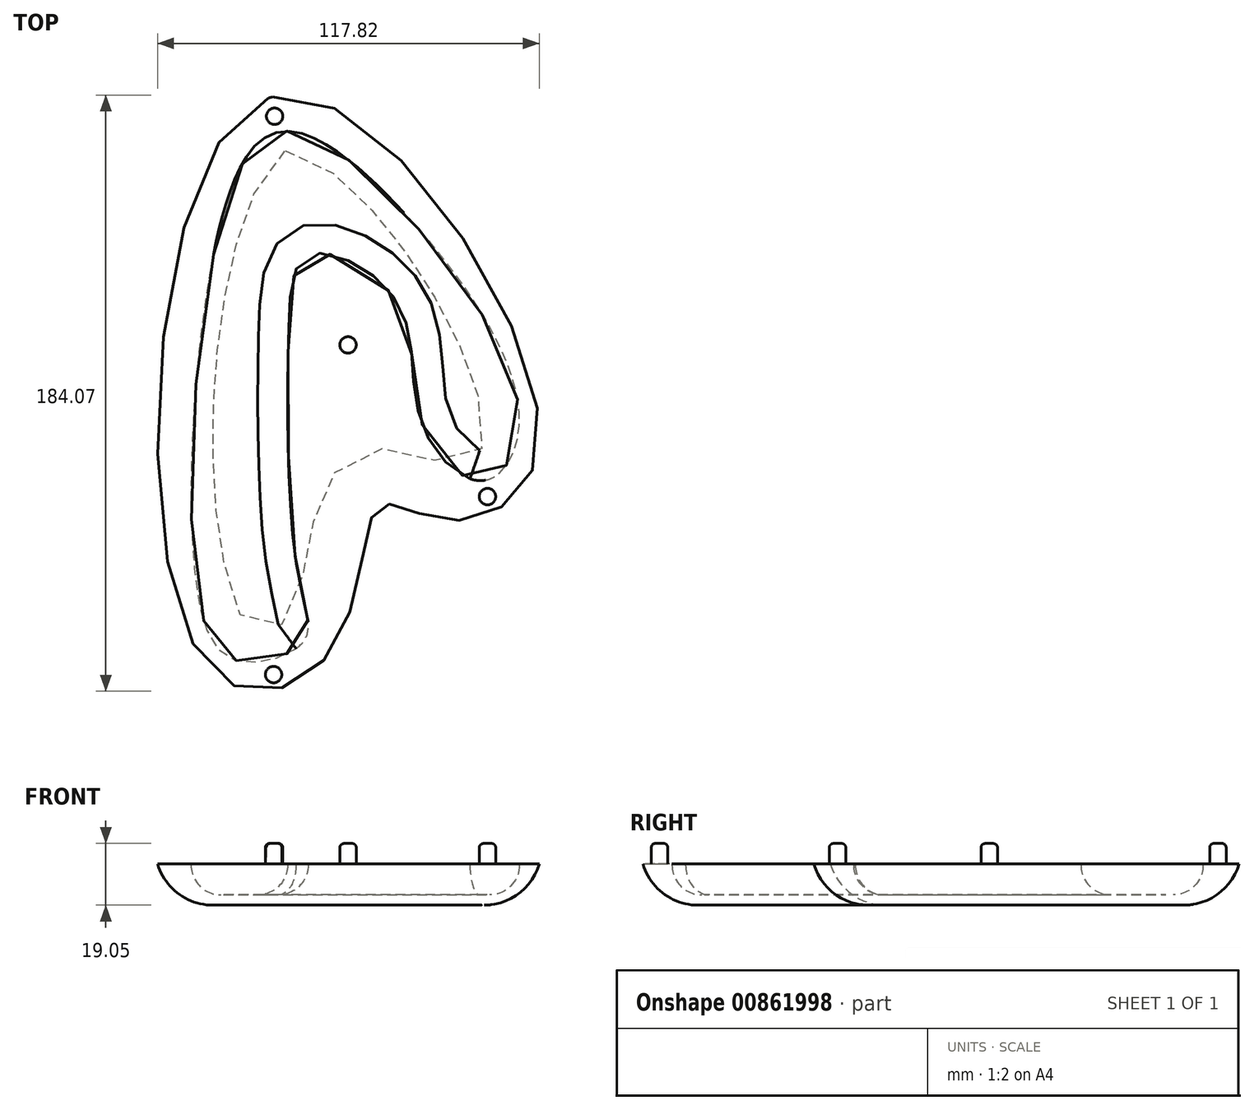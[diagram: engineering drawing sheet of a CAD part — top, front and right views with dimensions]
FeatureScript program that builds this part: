
annotation { "Feature Type Name" : "Feature", "Feature Type Description" : "" }
export const myFeature = defineFeature(function(context is Context, id is Id, definition is map)
    precondition{}
    {
        {
            var Q0;
            Q0=qCreatedBy(makeId("Top.planeOp"),FACE);
            var sketch = newSketch(context, id + "F0", { "sketchPlane" : qUnion([Q0])});
            skLineSegment(sketch, "E0", {"start": v(-51.7, -50.28) * mm, "end": v(-51.7, 51.32) * mm});
            skLineSegment(sketch, "E1", {"start": v(-51.7, 51.32) * mm, "end": v(-41.03, 51.32) * mm});
            skLineSegment(sketch, "E2", {"start": v(-41.03, 51.32) * mm, "end": v(-41.03, -50.28) * mm});
            skLineSegment(sketch, "E3", {"start": v(-41.03, -50.28) * mm, "end": v(-51.7, -50.28) * mm});
            skFitSpline(sketch, "E4", {"points": [v(-56.83, 61.26) * mm, v(-59.56, -52.95) * mm, v(-46.25, -64.69) * mm, v(-28.88, -58.06) * mm, v(-30.58, -38.29) * mm, v(-33.65, 37.4) * mm, v(-26.5, 61.26) * mm, v(0, 46.26) * mm, v(7.26, 9.44) * mm, v(26.35, -8.63) * mm, v(37.6, 11.15) * mm, v(2.49, 73.54) * mm, v(-36.38, 99.1) * mm, v(-56.83, 61.26) * mm]});
            skSolve(sketch);
        }
        {
            var Q0;
            Q0=makeQuery(id+"F0.imprint","IMPRINT",FACE,{"disambiguationData":[TD([[makeQuery(id+"F0.imprint","IMPRINT",EDGE,{"derivedFrom":sQuery(id+"F0.wireOp",EDGE,"E0")}),1.0]])]});
            var Q1;
            Q1=makeQuery(id+"F0.imprint","IMPRINT",FACE,{"disambiguationData":[TD([[makeQuery(id+"F0.imprint","IMPRINT",EDGE,{"derivedFrom":sQuery(id+"F0.wireOp",EDGE,"E0")}),-1.0]])]});
            extrude(context, id + "F1", {"entities" : qUnion([Q0, Q1]), "endBound" : BoundingType.SYMMETRIC, "depth" : 19.05 * mm, "offsetDistance" : 25.4 * mm});
        }
        {
            var Q0;
            Q0=makeQuery(id+"F1.opExtrude","CAP_FACE",FACE,{"disambiguationData":[OSD([sQuery(id+"F0.wireOp",EDGE,"E4")])],"isStart":false});
            fillet(context, id + "F2", {"entities" : qUnion([Q0]), "radius" : 9.22 * mm, "tangentPropagation" : true, "allowEdgeOverflow" : false});
        }
        {
            var Q0;
            Q0=makeQuery(id+"F1.opExtrude","CAP_FACE",FACE,{"disambiguationData":[OSD([sQuery(id+"F0.wireOp",EDGE,"E4")])],"isStart":true});
            fillet(context, id + "F3", {"entities" : qUnion([Q0]), "radius" : 9.22 * mm, "tangentPropagation" : true, "allowEdgeOverflow" : false});
        }
        {
            var Q0;
            Q0=qCreatedBy(makeId("Top.planeOp"),FACE);
            var sketch = newSketch(context, id + "F4", { "sketchPlane" : qUnion([Q0])});
            skFitSpline(sketch, "E5", {"points": [v(-39.96, 109.45) * mm, v(-60.26, -63.74) * mm, v(-19.95, -60.52) * mm, v(-5.79, -16.66) * mm, v(13.96, -20.7) * mm, v(43.72, 4.73) * mm, v(-39.96, 109.45) * mm]});
            skCircle(sketch, "E6", {"center": v(-15.3, 33.26) * mm, "radius": 2.54 * mm});
            skCircle(sketch, "E7", {"center": v(-38.28, -68.53) * mm, "radius": 2.54 * mm});
            skCircle(sketch, "E8", {"center": v(27.76, -13.57) * mm, "radius": 2.54 * mm});
            skCircle(sketch, "E9", {"center": v(-37.98, 103.86) * mm, "radius": 2.54 * mm});
            skSolve(sketch);
        }
        {
            var Q0;
            Q0=makeQuery(id+"F4.imprint","IMPRINT",FACE,{"disambiguationData":[TD([[makeQuery(id+"F4.imprint","IMPRINT",EDGE,{"derivedFrom":sQuery(id+"F4.wireOp",EDGE,"E5")}),1.0]])]});
            var Q1;
            Q1=makeQuery(id+"F4.imprint","IMPRINT",FACE,{"disambiguationData":[TD([[makeQuery(id+"F4.imprint","IMPRINT",EDGE,{"derivedFrom":sQuery(id+"F4.wireOp",EDGE,"E7")}),1.0]])]});
            var Q2;
            Q2=makeQuery(id+"F4.imprint","IMPRINT",FACE,{"disambiguationData":[TD([[makeQuery(id+"F4.imprint","IMPRINT",EDGE,{"derivedFrom":sQuery(id+"F4.wireOp",EDGE,"E6")}),1.0]])]});
            var Q3;
            Q3=makeQuery(id+"F4.imprint","IMPRINT",FACE,{"disambiguationData":[TD([[makeQuery(id+"F4.imprint","IMPRINT",EDGE,{"derivedFrom":sQuery(id+"F4.wireOp",EDGE,"E8")}),1.0]])]});
            var Q4;
            Q4=makeQuery(id+"F4.imprint","IMPRINT",FACE,{"disambiguationData":[TD([[makeQuery(id+"F4.imprint","IMPRINT",EDGE,{"derivedFrom":sQuery(id+"F4.wireOp",EDGE,"E9")}),1.0]])]});
            extrude(context, id + "F5", {"entities" : qUnion([Q0, Q1, Q2, Q3, Q4]), "oppositeDirection" : true, "depth" : 12.7 * mm, "offsetDistance" : 25.4 * mm});
        }
        {
            var Q0;
            Q0=makeQuery(id+"F4.imprint","IMPRINT",FACE,{"disambiguationData":[TD([[makeQuery(id+"F4.imprint","IMPRINT",EDGE,{"derivedFrom":sQuery(id+"F4.wireOp",EDGE,"E7")}),1.0]])]});
            var Q1;
            Q1=makeQuery(id+"F4.imprint","IMPRINT",FACE,{"disambiguationData":[TD([[makeQuery(id+"F4.imprint","IMPRINT",EDGE,{"derivedFrom":sQuery(id+"F4.wireOp",EDGE,"E6")}),1.0]])]});
            var Q2;
            Q2=makeQuery(id+"F4.imprint","IMPRINT",FACE,{"disambiguationData":[TD([[makeQuery(id+"F4.imprint","IMPRINT",EDGE,{"derivedFrom":sQuery(id+"F4.wireOp",EDGE,"E8")}),1.0]])]});
            var Q3;
            Q3=makeQuery(id+"F4.imprint","IMPRINT",FACE,{"disambiguationData":[TD([[makeQuery(id+"F4.imprint","IMPRINT",EDGE,{"derivedFrom":sQuery(id+"F4.wireOp",EDGE,"E9")}),1.0]])]});
            extrude(context, id + "F6", {"entities" : qUnion([Q0, Q1, Q2, Q3]), "operationType" : NewBodyOperationType.ADD, "depth" : 6.35 * mm, "offsetDistance" : 25.4 * mm});
        }
        {
            var Q0;
            Q0=makeQuery(id+"F1.opExtrude","SWEPT_BODY",BODY,{"disambiguationData":[OSD([sQuery(id+"F0.wireOp",EDGE,"E4")])]});
            var Q1;
            Q1=makeQuery(id+"F5.opExtrude","SWEPT_BODY",BODY,{"disambiguationData":[OSD([sQuery(id+"F4.wireOp",EDGE,"E5")])]});
            booleanBodies(context, id + "F7", {"operationType" : BooleanOperationType.SUBTRACTION, "tools" : qUnion([Q0]), "targets" : qUnion([Q1])});
        }
        {
            var Q0;
            Q0=makeQuery(id+"F5.opExtrude","CAP_FACE",FACE,{"disambiguationData":[OSD([sQuery(id+"F4.wireOp",EDGE,"E5")])],"isStart":false});
            fillet(context, id + "F8", {"entities" : qUnion([Q0]), "radius" : 17.78 * mm, "tangentPropagation" : true, "allowEdgeOverflow" : false});
        }
        {
            var Q0;
            Q0=makeQuery(id+"F6.opExtrude","CAP_EDGE",EDGE,{"disambiguationData":[OSD([sQuery(id+"F4.wireOp",EDGE,"E7")])],"isStart":false});
            var Q1;
            Q1=makeQuery(id+"F6.opExtrude","CAP_EDGE",EDGE,{"disambiguationData":[OSD([sQuery(id+"F4.wireOp",EDGE,"E6")])],"isStart":false});
            var Q2;
            Q2=makeQuery(id+"F6.opExtrude","CAP_EDGE",EDGE,{"disambiguationData":[OSD([sQuery(id+"F4.wireOp",EDGE,"E8")])],"isStart":false});
            var Q3;
            Q3=makeQuery(id+"F6.opExtrude","CAP_EDGE",EDGE,{"disambiguationData":[OSD([sQuery(id+"F4.wireOp",EDGE,"E9")])],"isStart":false});
            fillet(context, id + "F9", {"entities" : qUnion([Q0, Q1, Q2, Q3]), "radius" : 1.27 * mm, "tangentPropagation" : true, "allowEdgeOverflow" : false});
        }
    });
